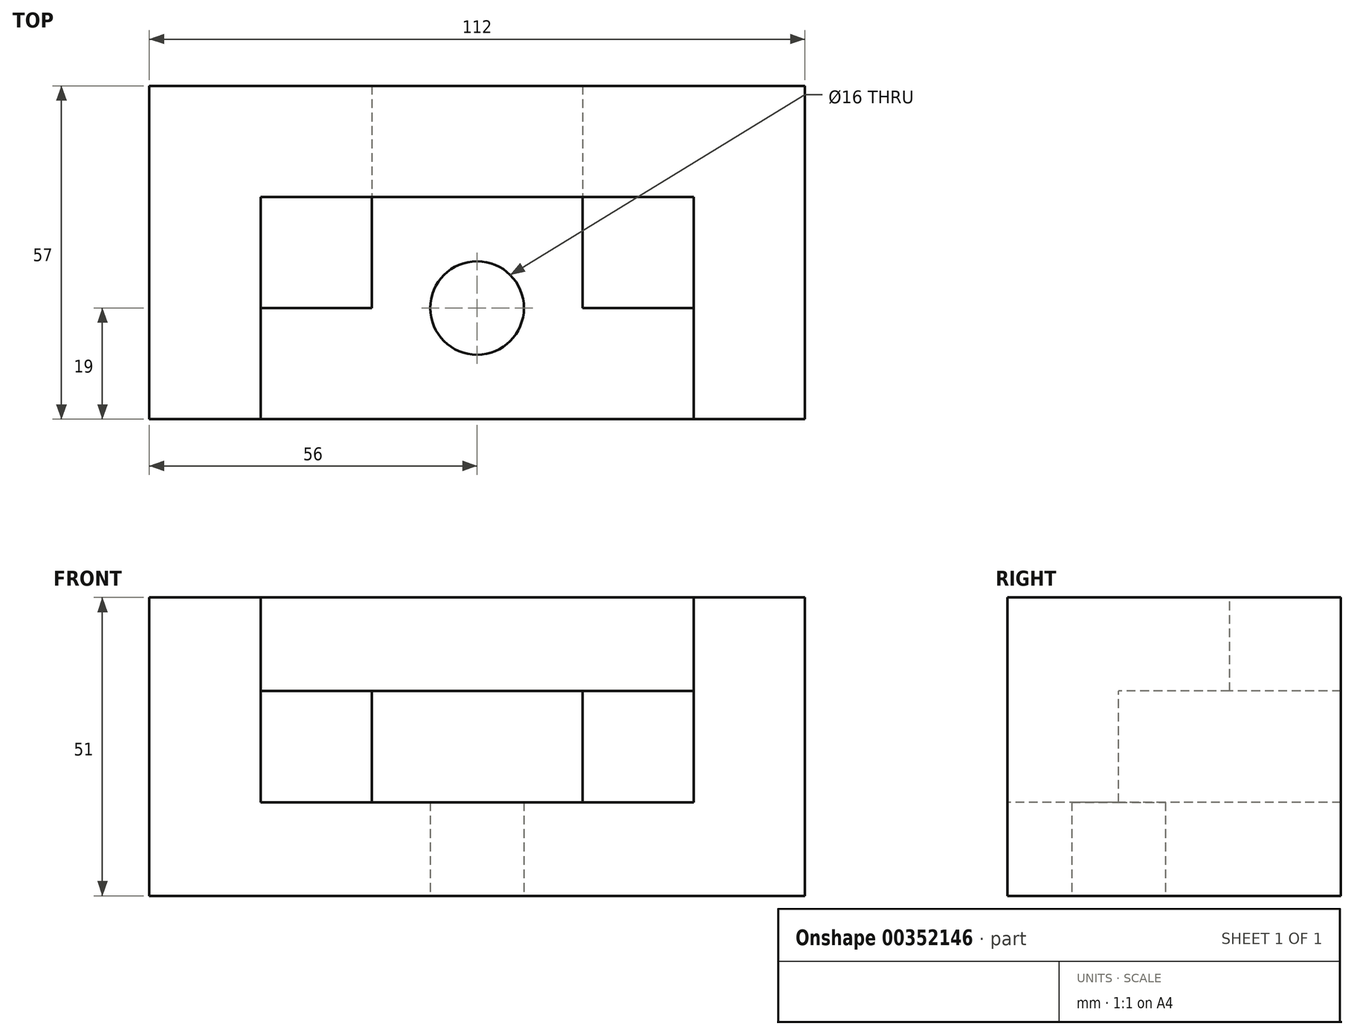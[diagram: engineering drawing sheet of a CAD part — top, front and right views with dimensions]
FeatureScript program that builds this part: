
annotation { "Feature Type Name" : "Feature", "Feature Type Description" : "" }
export const myFeature = defineFeature(function(context is Context, id is Id, definition is map)
    precondition{}
    {
        {
            var Q0;
            Q0=qCreatedBy(makeId("Front.planeOp"),FACE);
            var sketch = newSketch(context, id + "F0", { "sketchPlane" : qUnion([Q0])});
            skLineSegment(sketch, "E0", {"start": v(0, 0) * mm, "end": v(112, 0) * mm});
            skLineSegment(sketch, "E1", {"start": v(112, 0) * mm, "end": v(112, 51) * mm});
            skLineSegment(sketch, "E2", {"start": v(112, 51) * mm, "end": v(93, 51) * mm});
            skLineSegment(sketch, "E3", {"start": v(93, 51) * mm, "end": v(93, 16) * mm});
            skLineSegment(sketch, "E4", {"start": v(93, 16) * mm, "end": v(19, 16) * mm});
            skLineSegment(sketch, "E5", {"start": v(19, 16) * mm, "end": v(19, 51) * mm});
            skLineSegment(sketch, "E6", {"start": v(19, 51) * mm, "end": v(0, 51) * mm});
            skLineSegment(sketch, "E7", {"start": v(0, 51) * mm, "end": v(0, 0) * mm});
            skLineSegment(sketch, "E8", {"start": v(19, 35) * mm, "end": v(93, 35) * mm});
            skLineSegment(sketch, "E9", {"start": v(74, 35) * mm, "end": v(74, 16) * mm});
            skLineSegment(sketch, "E10", {"start": v(38, 35) * mm, "end": v(38, 16) * mm});
            skLineSegment(sketch, "E11", {"start": v(19, 51) * mm, "end": v(93, 51) * mm});
            skSolve(sketch);
        }
        {
            var Q0;
            {var subQ4=sQuery(id+"F0.wireOp",EDGE,"E11");Q0=makeQuery(id+"F0.imprint","IMPRINT",FACE,{"disambiguationData":[TD([[makeQuery(id+"F0.imprint","IMPRINT",EDGE,{"derivedFrom":subQ4}),-1.0]])]});}
            extrude(context, id + "F1", {"entities" : qUnion([Q0]), "oppositeDirection" : true, "depth" : 57 * mm, "hasSecondDirection" : true, "secondDirectionOppositeDirection" : true, "secondDirectionDepth" : 38 * mm});
        }
        {
            var Q0;
            Q0=makeQuery(id+"F0.imprint","IMPRINT",FACE,{"disambiguationData":[TD([[makeQuery(id+"F0.imprint","IMPRINT",EDGE,{"derivedFrom":sQuery(id+"F0.wireOp",EDGE,"E0")}),1.0]])]});
            extrude(context, id + "F2", {"entities" : qUnion([Q0]), "operationType" : NewBodyOperationType.ADD, "oppositeDirection" : true, "depth" : 57 * mm});
        }
        {
            var Q0;
            {var subQ5=sQuery(id+"F0.wireOp",EDGE,"E9");Q0=makeQuery(id+"F0.imprint","IMPRINT",FACE,{"disambiguationData":[TD([[makeQuery(id+"F0.imprint","IMPRINT",EDGE,{"derivedFrom":subQ5}),1.0]])]});}
            var Q1;
            {var subQ3=sQuery(id+"F0.wireOp",EDGE,"E10");Q1=makeQuery(id+"F0.imprint","IMPRINT",FACE,{"disambiguationData":[TD([[makeQuery(id+"F0.imprint","IMPRINT",EDGE,{"derivedFrom":subQ3}),-1.0]])]});}
            extrude(context, id + "F3", {"entities" : qUnion([Q0, Q1]), "operationType" : NewBodyOperationType.ADD, "oppositeDirection" : true, "depth" : 57 * mm, "hasSecondDirection" : true, "secondDirectionOppositeDirection" : true, "secondDirectionDepth" : 19 * mm});
        }
        {
            var Q0;
            Q0=makeQuery(id+"F2.opExtrude","SWEPT_FACE",FACE,{"disambiguationData":[OSD([sQuery(id+"F0.wireOp",EDGE,"E0")])]});
            var sketch = newSketch(context, id + "F4", { "sketchPlane" : qUnion([Q0])});
            skPoint(sketch, "E12", {"position": v(56, -19) * mm});
            skPoint(sketch, "E12.positionSnap0", {"position": v(56, 0) * mm});
            skCircle(sketch, "E13", {"center": v(56, -19) * mm, "radius": 8 * mm});
            skSolve(sketch);
        }
        {
            var Q0;
            Q0=makeQuery(id+"F4.imprint","IMPRINT",FACE,{"disambiguationData":[TD([[makeQuery(id+"F4.imprint","IMPRINT",EDGE,{"derivedFrom":sQuery(id+"F4.wireOp",EDGE,"E13")}),1.0]])]});
            extrude(context, id + "F5", {"entities" : qUnion([Q0]), "operationType" : NewBodyOperationType.REMOVE, "oppositeDirection" : true, "depth" : 16 * mm});
        }
    });
